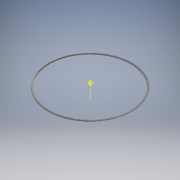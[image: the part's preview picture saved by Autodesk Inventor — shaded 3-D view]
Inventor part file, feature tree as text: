
AUTODESK INVENTOR PART (.ipt)
format: ipt  version: 2017 (Build 210142000, 142)  size: 2,474,496 bytes
history: native  units: mm
features: other x24, loft x2, pattern_circular x2, sketch x2, extrude x1
ambient origin geometry x6: Origin, XZ Plane, X Axis, Y Axis, Z Axis, Center Point
bodies: Solid1 (feature_tree)
feature tree (31):
  other  "Top Point"
  other  "Mesh Plane2"
  other  "Teeth Body"
  other  "Start Point"
  other  "Tooth Plane"
  other  "Start Sketch"
  other  "End Point"
  other  "3D Sketch Right"
  other  "End Plane Right"
  loft  "Loft Right"
  pattern_circular  "Circular Pattern Right"  [2 undecoded]
  other  "3D Sketch Left"
  other  "End Plane Left"
  loft  "Loft Left"
  pattern_circular  "Circular Pattern Left"  Angle=90.0deg  [1 undecoded]
  other  "Fix Body"
  extrude  "Extrusion1"  Depth=10.0mm
  other  "Mesh Plane"
  other  "Top Plane"
  other  "Teeth Body Sketch"
  other  "End Plane"
  other  "End Sketch"
  other  "Helical Curve Left"
  other  "End Sketch Left"
  other  "Body Sketch"
  sketch  "Sketch6"  dims[d0=289.56mm d1=289.245872mm]
  other  "Srf1"
  other  "Helical Curve Right"
  other  "End Sketch Right"
  sketch  "Sketch8"  dims[d2=289.767443mm d3=5.08mm d4=8.681968mm d5=90.0deg d7=874.034304mm d8=801.120004mm d9=1715.454893mm d11=5.266267mm d12=843.193974mm d15=772.852458mm d16=1654.925008mm d17=0.0mm d18=90.0deg d19=0.0mm d20=90.0deg d21=1710.0mm d22=360.0deg d26=126.354884mm d27=0.368656mm d28=289.56mm d29=-15.007357mm d30=843.193974mm d31=772.852458mm d32=1654.925008mm d35=0.0mm d37=0.0mm d39=0.0mm d40=90.0deg d41=1710.0mm d42=360.0deg d46=90.0deg d47=90.0deg d48=0.0mm d49=0.0mm d50=90.0deg d51=0.183719mm d52=0.0mm d53=0.0mm d54=0.0mm d56=9.838623mm d57=2070.788026mm d58=2065.498052mm d59=1997.720199mm d60=1992.616883mm d61=1997.720199mm d62=1992.616883mm d63=90.0deg d64=90.0deg d65=126.354884mm d66=31.5mm d67=289.56mm d68=-15.007357mm d69=0.368656mm d70=772.852458mm d71=1654.925008mm d72=843.193974mm d73=1992.616883mm d74=1997.720199mm d75=0.0mm d76=90.0deg d77=0.0mm d78=90.0deg d79=0.0mm d80=90.0deg d81=1710.0mm d82=360.0deg d84=10.0mm d85=20.0mm d86=20.0mm d87=10.0mm d88=0.0mm d89=0.0mm d90=25.4mm d91=0.0mm]
  other  "Pitch Diameter"
note: 3 required parameter values undecoded (feature->parameter linkage not recoverable at this tier; creation-order binding heuristic only, values carry confidence <= 0.55)
